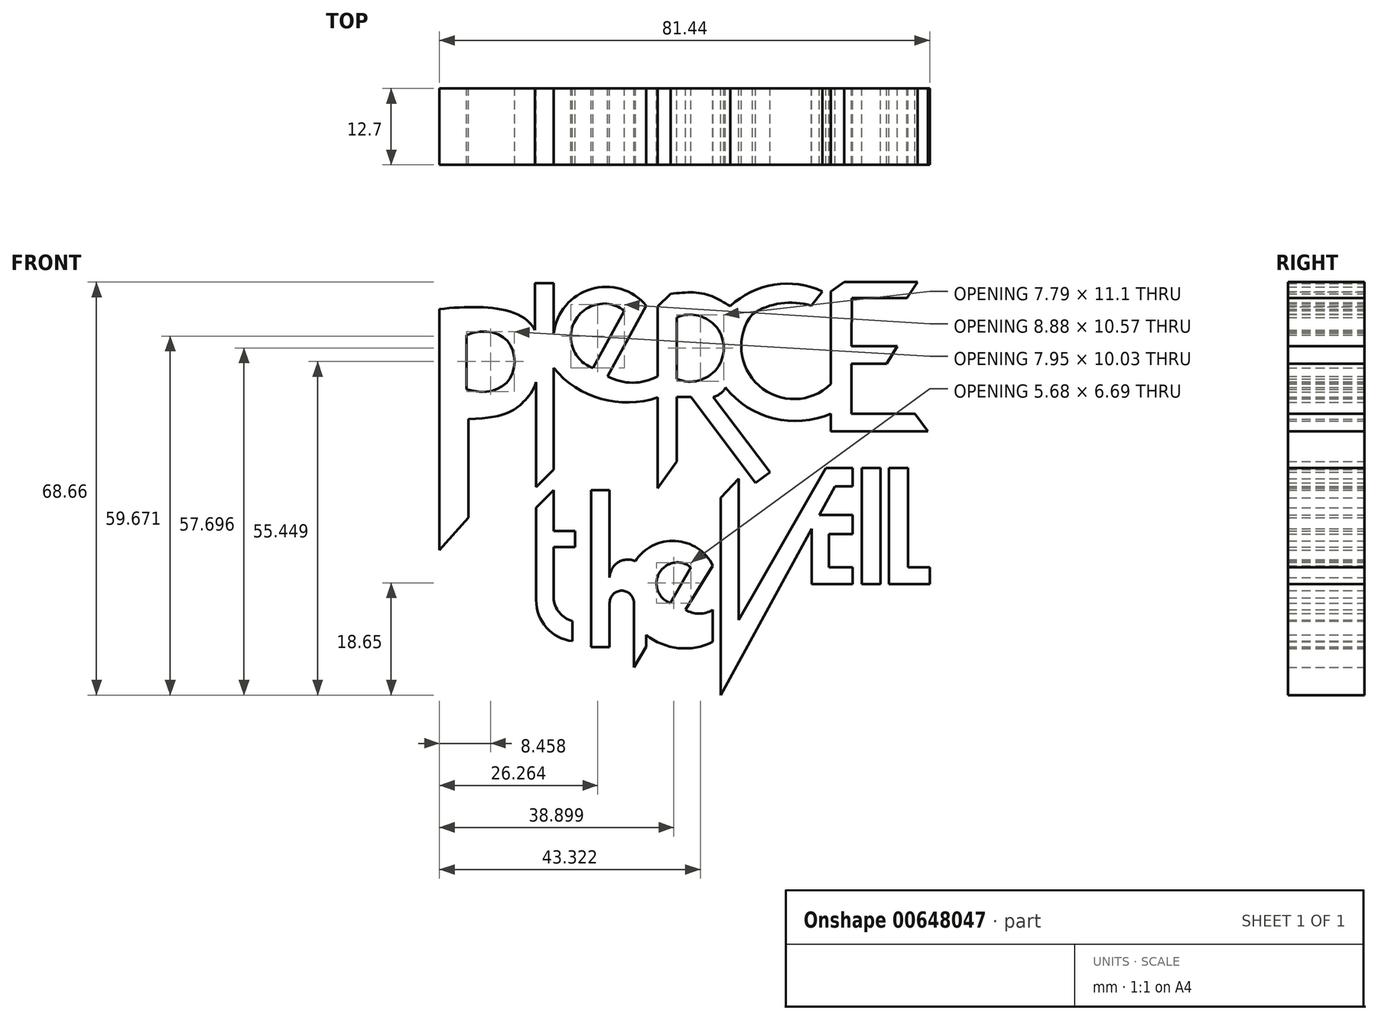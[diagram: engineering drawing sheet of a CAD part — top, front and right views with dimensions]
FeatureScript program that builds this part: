
annotation { "Feature Type Name" : "Feature", "Feature Type Description" : "" }
export const myFeature = defineFeature(function(context is Context, id is Id, definition is map)
    precondition{}
    {
        {
            var Q0;
            Q0=qCreatedBy(makeId("Front.planeOp"),FACE);
            var sketch = newSketch(context, id + "F0", { "sketchPlane" : qUnion([Q0])});
            skLineSegment(sketch, "E0", {"start": v(-41.74, 42.95) * mm, "end": v(-41.74, 2.85) * mm});
            skLineSegment(sketch, "E1", {"start": v(-41.74, 2.85) * mm, "end": v(-36.93, 8.26) * mm});
            skLineSegment(sketch, "E2", {"start": v(-36.93, 8.26) * mm, "end": v(-36.93, 24.66) * mm});
            skFitSpline(sketch, "E3", {"points": [v(-41.74, 42.95) * mm, v(-31.77, 42.95) * mm, v(-25.89, 39.42) * mm, v(-25.68, 30.79) * mm, v(-28.24, 27.1) * mm, v(-36.93, 24.66) * mm], "startDerivative": vector(45.06, 4.31) * mm, "endDerivative": vector(-79.1, -2.73) * mm});
            skLineSegment(sketch, "E4", {"start": v(-37.26, 38.63) * mm, "end": v(-37.26, 29.61) * mm});
            skFitSpline(sketch, "E5", {"points": [v(-37.26, 38.63) * mm, v(-31.77, 38.63) * mm, v(-29.42, 35.5) * mm, v(-30.2, 31.18) * mm, v(-33.73, 29.22) * mm, v(-37.26, 29.61) * mm], "startDerivative": vector(25.13, 10.74) * mm, "endDerivative": vector(-18.9, 4.53) * mm});
            skLineSegment(sketch, "E6", {"start": v(-25.89, 39.42) * mm, "end": v(-25.89, 47.26) * mm});
            skLineSegment(sketch, "E7", {"start": v(-25.89, 47.26) * mm, "end": v(-22.8, 47.26) * mm});
            skLineSegment(sketch, "E8", {"start": v(-22.8, 47.26) * mm, "end": v(-22.8, 16.24) * mm});
            skLineSegment(sketch, "E9", {"start": v(-22.8, 16.24) * mm, "end": v(-25.68, 13.34) * mm});
            skLineSegment(sketch, "E10", {"start": v(-25.68, 13.34) * mm, "end": v(-25.68, 30.79) * mm});
            skPoint(sketch, "E11.1.internal.snap0", {"position": v(-25.89, 43.34) * mm});
            skLineSegment(sketch, "E12", {"start": v(-7.38, 43.53) * mm, "end": v(-13.83, 31.78) * mm});
            skLineSegment(sketch, "E13", {"start": v(-5.5, 31.78) * mm, "end": v(-5.5, 43.4) * mm});
            skLineSegment(sketch, "E14", {"start": v(-5.5, 43.4) * mm, "end": v(-3.37, 45.48) * mm});
            skLineSegment(sketch, "E15", {"start": v(-5.5, 31.78) * mm, "end": v(-5.5, 13.15) * mm});
            skLineSegment(sketch, "E16", {"start": v(-5.5, 13.15) * mm, "end": v(-2.31, 17.61) * mm});
            skLineSegment(sketch, "E17", {"start": v(-2.31, 17.61) * mm, "end": v(-2.31, 28.33) * mm});
            skPoint(sketch, "E18.2.internal.snap0", {"position": v(-10.6, 37.65) * mm});
            skArc(sketch, "E19", {"start": v(-22.8, 39.1) * mm, "mid": v(-22.79, 39.01) * mm, "end": v(-22.78, 38.92) * mm});
            skArc(sketch, "E20", {"start": v(-13.83, 31.78) * mm, "mid": v(-9.67, 30.7) * mm, "end": v(-5.5, 31.78) * mm});
            skArc(sketch, "E21", {"start": v(-7.38, 43.53) * mm, "mid": v(-16.67, 46.23) * mm, "end": v(-22.8, 38.76) * mm});
            skLineSegment(sketch, "E22", {"start": v(-11.04, 42.65) * mm, "end": v(-16.26, 33.14) * mm});
            skArc(sketch, "E23", {"start": v(-11.04, 42.65) * mm, "mid": v(-19.25, 40.97) * mm, "end": v(-16.26, 33.14) * mm});
            skArc(sketch, "E24", {"start": v(-22.8, 33.14) * mm, "mid": v(-14.9, 28.02) * mm, "end": v(-5.5, 28.25) * mm});
            skLineSegment(sketch, "E25", {"start": v(-2.31, 41.56) * mm, "end": v(-2.31, 31.33) * mm});
            skLineSegment(sketch, "E26", {"start": v(-2.31, 28.33) * mm, "end": v(0, 28.33) * mm});
            skArc(sketch, "E27", {"start": v(-2.31, 31.33) * mm, "mid": v(5.48, 36.45) * mm, "end": v(-2.31, 41.56) * mm});
            skFitSpline(sketch, "E28", {"points": [v(-3.37, 45.48) * mm, v(2.24, 45.48) * mm, v(6.55, 43.42) * mm], "startDerivative": vector(11.27, 1.12) * mm, "endDerivative": vector(8.56, -5.32) * mm});
            skLineSegment(sketch, "E29", {"start": v(0, 28.33) * mm, "end": v(10.77, 14.02) * mm});
            skLineSegment(sketch, "E30", {"start": v(10.77, 14.02) * mm, "end": v(13.15, 15.81) * mm});
            skLineSegment(sketch, "E31", {"start": v(13.15, 15.81) * mm, "end": v(3.73, 28.33) * mm});
            skArc(sketch, "E32", {"start": v(21.89, 45.85) * mm, "mid": v(13.85, 46.98) * mm, "end": v(6.55, 43.42) * mm});
            skLineSegment(sketch, "E33", {"start": v(21.89, 45.85) * mm, "end": v(20.03, 43.5) * mm});
            skArc(sketch, "E34", {"start": v(20.03, 43.5) * mm, "mid": v(14.97, 43.9) * mm, "end": v(10.22, 42.1) * mm});
            skArc(sketch, "E35", {"start": v(10.22, 42.1) * mm, "mid": v(8.43, 35.98) * mm, "end": v(11.26, 30.26) * mm});
            skArc(sketch, "E36", {"start": v(11.26, 30.26) * mm, "mid": v(17.3, 27.98) * mm, "end": v(23.27, 30.46) * mm});
            skLineSegment(sketch, "E37", {"start": v(23.27, 30.46) * mm, "end": v(23.27, 45.85) * mm});
            skLineSegment(sketch, "E38", {"start": v(23.27, 45.85) * mm, "end": v(25.47, 47.41) * mm});
            skLineSegment(sketch, "E39", {"start": v(23.27, 30.46) * mm, "end": v(23.27, 22.6) * mm});
            skLineSegment(sketch, "E40", {"start": v(23.27, 22.6) * mm, "end": v(39.4, 22.6) * mm});
            skLineSegment(sketch, "E41", {"start": v(26.66, 25.53) * mm, "end": v(26.66, 33.85) * mm});
            skLineSegment(sketch, "E42", {"start": v(26.66, 33.85) * mm, "end": v(32.55, 33.85) * mm});
            skLineSegment(sketch, "E43", {"start": v(32.55, 33.85) * mm, "end": v(34.33, 36.78) * mm});
            skLineSegment(sketch, "E44", {"start": v(34.33, 36.78) * mm, "end": v(26.66, 36.78) * mm});
            skLineSegment(sketch, "E45", {"start": v(25.47, 47.41) * mm, "end": v(37.67, 47.41) * mm});
            skLineSegment(sketch, "E46", {"start": v(37.67, 47.41) * mm, "end": v(35.9, 44.75) * mm});
            skLineSegment(sketch, "E47", {"start": v(35.9, 44.75) * mm, "end": v(26.78, 44.75) * mm});
            skLineSegment(sketch, "E48", {"start": v(26.66, 36.78) * mm, "end": v(26.78, 44.75) * mm});
            skLineSegment(sketch, "E49", {"start": v(26.66, 25.53) * mm, "end": v(37.24, 25.53) * mm});
            skLineSegment(sketch, "E50", {"start": v(37.24, 25.53) * mm, "end": v(39.4, 22.6) * mm});
            skArc(sketch, "E51", {"start": v(5.74, 29.91) * mm, "mid": v(13.76, 24.75) * mm, "end": v(23.27, 25.55) * mm});
            skFitSpline(sketch, "E52", {"points": [v(3.73, 28.33) * mm, v(5.74, 29.91) * mm], "startDerivative": vector(2.22, 0.32) * mm, "endDerivative": vector(0.47, 1.9) * mm});
            skLineSegment(sketch, "E53", {"start": v(-22.8, 12.83) * mm, "end": v(-25.68, 9.93) * mm});
            skLineSegment(sketch, "E54", {"start": v(-25.68, 9.93) * mm, "end": v(-25.68, -5.48) * mm});
            skLineSegment(sketch, "E55", {"start": v(-22.8, 12.83) * mm, "end": v(-22.8, 6.03) * mm});
            skLineSegment(sketch, "E56", {"start": v(-22.8, 6.03) * mm, "end": v(-19.23, 6.03) * mm});
            skLineSegment(sketch, "E57", {"start": v(-19.23, 6.03) * mm, "end": v(-19.23, 3.4) * mm});
            skLineSegment(sketch, "E58", {"start": v(-19.23, 3.4) * mm, "end": v(-22.8, 3.4) * mm});
            skLineSegment(sketch, "E59", {"start": v(-22.8, 3.4) * mm, "end": v(-22.8, -5.06) * mm});
            skArc(sketch, "E60", {"start": v(-22.8, -5.06) * mm, "mid": v(-21.85, -7.51) * mm, "end": v(-19.65, -8.95) * mm});
            skArc(sketch, "E61", {"start": v(-25.68, -5.48) * mm, "mid": v(-23.96, -10.02) * mm, "end": v(-19.65, -12.27) * mm});
            skLineSegment(sketch, "E62", {"start": v(-19.65, -8.95) * mm, "end": v(-19.65, -12.27) * mm});
            skLineSegment(sketch, "E63", {"start": v(-16.53, 6.03) * mm, "end": v(-16.53, 12.83) * mm});
            skLineSegment(sketch, "E64", {"start": v(-16.53, 12.83) * mm, "end": v(-13.48, 12.83) * mm});
            skLineSegment(sketch, "E65", {"start": v(-13.48, 12.83) * mm, "end": v(-13.48, -1.73) * mm});
            skLineSegment(sketch, "E66", {"start": v(-16.53, 6.03) * mm, "end": v(-16.53, -13.24) * mm});
            skLineSegment(sketch, "E67", {"start": v(-16.53, -13.24) * mm, "end": v(-13.48, -13.24) * mm});
            skLineSegment(sketch, "E68", {"start": v(-13.48, -13.24) * mm, "end": v(-13.48, -5.9) * mm});
            skArc(sketch, "E69", {"start": v(-7.43, -1.73) * mm, "mid": v(-10.45, 1.3) * mm, "end": v(-13.48, -1.73) * mm});
            skLineSegment(sketch, "E70", {"start": v(-7.43, -1.73) * mm, "end": v(-7.43, -13.23) * mm});
            skLineSegment(sketch, "E71", {"start": v(-7.43, -13.23) * mm, "end": v(-9.46, -16.62) * mm});
            skLineSegment(sketch, "E72", {"start": v(-9.46, -16.62) * mm, "end": v(-9.46, -5.9) * mm});
            skArc(sketch, "E73", {"start": v(-9.46, -5.9) * mm, "mid": v(-11.47, -3.88) * mm, "end": v(-13.48, -5.9) * mm});
            skLineSegment(sketch, "E74", {"start": v(-0.89, -7.06) * mm, "end": v(3.67, 0.28) * mm});
            skLineSegment(sketch, "E75", {"start": v(-3.4, -5.94) * mm, "end": v(0, 0) * mm});
            skArc(sketch, "E76", {"start": v(0, 0) * mm, "mid": v(-5.23, -0.95) * mm, "end": v(-3.4, -5.94) * mm});
            skArc(sketch, "E77", {"start": v(3.67, 0.28) * mm, "mid": v(-2.55, 4.39) * mm, "end": v(-9.21, 1.03) * mm});
            skArc(sketch, "E78", {"start": v(-7.43, -11.21) * mm, "mid": v(-2.05, -13.44) * mm, "end": v(3.67, -12.4) * mm});
            skArc(sketch, "E79", {"start": v(-0.89, -7.06) * mm, "mid": v(1.4, -7.7) * mm, "end": v(3.67, -7.06) * mm});
            skLineSegment(sketch, "E80", {"start": v(22.41, 16.5) * mm, "end": v(26.86, 16.5) * mm});
            skLineSegment(sketch, "E81", {"start": v(26.86, 16.5) * mm, "end": v(26.86, 13.47) * mm});
            skLineSegment(sketch, "E82", {"start": v(26.86, 13.47) * mm, "end": v(23.97, 13.47) * mm});
            skLineSegment(sketch, "E83", {"start": v(23.97, 13.47) * mm, "end": v(21.37, 8.72) * mm});
            skLineSegment(sketch, "E84", {"start": v(21.37, 8.72) * mm, "end": v(26.86, 8.72) * mm});
            skLineSegment(sketch, "E85", {"start": v(26.86, 8.72) * mm, "end": v(26.86, 5.55) * mm});
            skLineSegment(sketch, "E86", {"start": v(26.86, 5.55) * mm, "end": v(22.94, 5.55) * mm});
            skLineSegment(sketch, "E87", {"start": v(22.94, 5.55) * mm, "end": v(22.94, 0) * mm});
            skLineSegment(sketch, "E88", {"start": v(22.94, 0) * mm, "end": v(26.86, 0) * mm});
            skLineSegment(sketch, "E89", {"start": v(26.86, 0) * mm, "end": v(26.86, -2.81) * mm});
            skLineSegment(sketch, "E90", {"start": v(26.86, -2.81) * mm, "end": v(20.11, -2.81) * mm});
            skLineSegment(sketch, "E91", {"start": v(20.11, 6.43) * mm, "end": v(20.11, -2.81) * mm});
            skLineSegment(sketch, "E92.trimOffspring", {"start": v(20.11, 6.43) * mm, "end": v(18.77, 3.98) * mm});
            skLineSegment(sketch, "E93", {"start": v(28.38, 16.5) * mm, "end": v(28.38, -2.81) * mm});
            skLineSegment(sketch, "E94", {"start": v(28.38, -2.81) * mm, "end": v(31.53, -2.81) * mm});
            skLineSegment(sketch, "E95", {"start": v(31.53, -2.81) * mm, "end": v(31.53, 16.5) * mm});
            skLineSegment(sketch, "E96", {"start": v(31.53, 16.5) * mm, "end": v(28.38, 16.5) * mm});
            skLineSegment(sketch, "E97", {"start": v(32.93, 16.5) * mm, "end": v(36.1, 16.5) * mm});
            skLineSegment(sketch, "E98", {"start": v(36.1, 16.5) * mm, "end": v(36.1, 0) * mm});
            skLineSegment(sketch, "E99", {"start": v(36.1, 0) * mm, "end": v(39.7, 0) * mm});
            skLineSegment(sketch, "E100", {"start": v(39.7, 0) * mm, "end": v(39.7, -2.81) * mm});
            skLineSegment(sketch, "E101", {"start": v(39.7, -2.81) * mm, "end": v(32.93, -2.81) * mm});
            skLineSegment(sketch, "E102", {"start": v(32.93, -2.81) * mm, "end": v(32.93, 16.5) * mm});
            skLineSegment(sketch, "E103", {"start": v(3.67, -7.06) * mm, "end": v(3.67, -12.4) * mm});
            skLineSegment(sketch, "E104", {"start": v(18.77, 3.98) * mm, "end": v(4.94, -21.25) * mm});
            skLineSegment(sketch, "E105", {"start": v(4.94, -21.25) * mm, "end": v(4.94, 11.56) * mm});
            skLineSegment(sketch, "E106", {"start": v(7.93, 14.76) * mm, "end": v(7.93, -8.75) * mm});
            skLineSegment(sketch, "E107", {"start": v(7.93, -8.75) * mm, "end": v(22.41, 16.5) * mm});
            skLineSegment(sketch, "E108", {"start": v(7.93, 14.76) * mm, "end": v(4.94, 11.56) * mm});
            skSolve(sketch);
        }
        {
            var Q0;
            Q0=makeQuery(id+"F0.imprint","IMPRINT",FACE,{"disambiguationData":[TD([[makeQuery(id+"F0.imprint","IMPRINT",EDGE,{"derivedFrom":sQuery(id+"F0.wireOp",EDGE,"E53")}),1.0]])]});
            var Q1;
            Q1=makeQuery(id+"F0.imprint","IMPRINT",FACE,{"disambiguationData":[TD([[makeQuery(id+"F0.imprint","IMPRINT",EDGE,{"derivedFrom":sQuery(id+"F0.wireOp",EDGE,"E93")}),1.0]])]});
            var Q2;
            Q2=makeQuery(id+"F0.imprint","IMPRINT",FACE,{"disambiguationData":[TD([[makeQuery(id+"F0.imprint","IMPRINT",EDGE,{"derivedFrom":sQuery(id+"F0.wireOp",EDGE,"E97")}),-1.0]])]});
            var Q3;
            {var subQ1=sQuery(id+"F0.wireOp",EDGE,"E37");Q3=makeQuery(id+"F0.imprint","IMPRINT",FACE,{"disambiguationData":[TD([[makeQuery(id+"F0.imprint","IMPRINT",EDGE,{"derivedFrom":subQ1}),-1.0]])]});}
            var Q4;
            Q4=makeQuery(id+"F0.imprint","IMPRINT",FACE,{"disambiguationData":[TD([[makeQuery(id+"F0.imprint","IMPRINT",EDGE,{"derivedFrom":sQuery(id+"F0.wireOp",EDGE,"E63")}),-1.0]])]});
            var Q5;
            {var subQ0=sQuery(id+"F0.wireOp",EDGE,"E19");Q5=makeQuery(id+"F0.imprint","IMPRINT",FACE,{"disambiguationData":[TD([[makeQuery(id+"F0.imprint","IMPRINT",EDGE,{"derivedFrom":subQ0}),-1.0]])]});}
            var Q6;
            {var subQ0=sQuery(id+"F0.wireOp",EDGE,"E74");Q6=makeQuery(id+"F0.imprint","IMPRINT",FACE,{"disambiguationData":[TD([[makeQuery(id+"F0.imprint","IMPRINT",EDGE,{"derivedFrom":subQ0}),-1.0]])]});}
            var Q7;
            {var subQ3=sQuery(id+"F0.wireOp",EDGE,"E6");Q7=makeQuery(id+"F0.imprint","IMPRINT",FACE,{"disambiguationData":[TD([[makeQuery(id+"F0.imprint","IMPRINT",EDGE,{"derivedFrom":subQ3}),-1.0]])]});}
            var Q8;
            {var subQ4=sQuery(id+"F0.wireOp",EDGE,"E13");Q8=makeQuery(id+"F0.imprint","IMPRINT",FACE,{"disambiguationData":[TD([[makeQuery(id+"F0.imprint","IMPRINT",EDGE,{"derivedFrom":subQ4}),-1.0]])]});}
            var Q9;
            {var subQ3=sQuery(id+"F0.wireOp",EDGE,"E12");Q9=makeQuery(id+"F0.imprint","IMPRINT",FACE,{"disambiguationData":[TD([[makeQuery(id+"F0.imprint","IMPRINT",EDGE,{"derivedFrom":subQ3}),-1.0]])]});}
            var Q10;
            Q10=makeQuery(id+"F0.imprint","IMPRINT",FACE,{"disambiguationData":[TD([[makeQuery(id+"F0.imprint","IMPRINT",EDGE,{"derivedFrom":sQuery(id+"F0.wireOp",EDGE,"E74")}),1.0]])]});
            var Q11;
            {var subQ6=sQuery(id+"F0.wireOp",EDGE,"JVwohNua-66uG-wDmT-Dddu-gcTOqGXHXycN");Q11=makeQuery(id+"F0.imprint","IMPRINT",FACE,{"disambiguationData":[TD([[makeQuery(id+"F0.imprint","IMPRINT",EDGE,{"derivedFrom":subQ6}),-1.0]])]});}
            var Q12;
            {var subQ1=sQuery(id+"F0.wireOp",EDGE,"E0");Q12=makeQuery(id+"F0.imprint","IMPRINT",FACE,{"disambiguationData":[TD([[makeQuery(id+"F0.imprint","IMPRINT",EDGE,{"derivedFrom":subQ1}),1.0]])]});}
            var Q13;
            Q13=makeQuery(id+"F0.imprint","IMPRINT",FACE,{"disambiguationData":[TD([[makeQuery(id+"F0.imprint","IMPRINT",EDGE,{"derivedFrom":sQuery(id+"F0.wireOp",EDGE,"E80")}),-1.0]])]});
            extrude(context, id + "F1", {"entities" : qUnion([Q0, Q1, Q2, Q3, Q4, Q5, Q6, Q7, Q8, Q9, Q10, Q11, Q12, Q13]), "depth" : 12.7 * mm, "offsetDistance" : 25.4 * mm});
        }
    });
